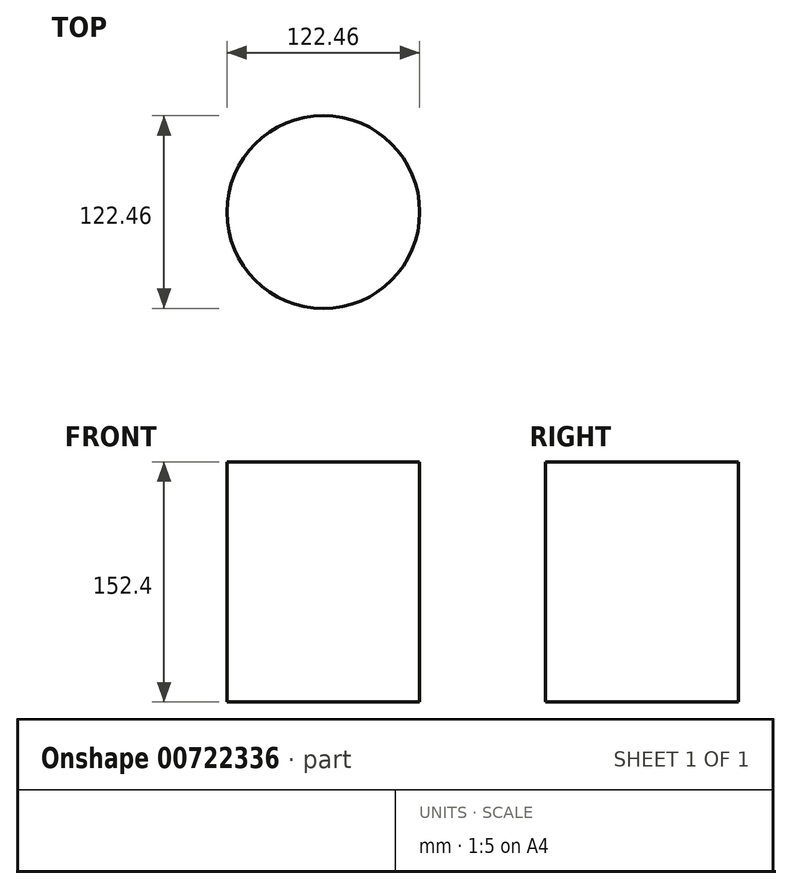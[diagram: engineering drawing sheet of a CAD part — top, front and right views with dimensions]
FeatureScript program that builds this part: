
annotation { "Feature Type Name" : "Feature", "Feature Type Description" : "" }
export const myFeature = defineFeature(function(context is Context, id is Id, definition is map)
    precondition{}
    {
        {
            var Q0;
            Q0=qCreatedBy(makeId("Top.planeOp"),FACE);
            var sketch = newSketch(context, id + "F0", { "sketchPlane" : qUnion([Q0])});
            skCircle(sketch, "E0", {"center": v(0, 0) * mm, "radius": 61.23 * mm});
            skSolve(sketch);
        }
        {
            var Q0;
            Q0=makeQuery(id+"F0.imprint","IMPRINT",FACE,{"disambiguationData":[TD([[makeQuery(id+"F0.imprint","IMPRINT",EDGE,{"derivedFrom":sQuery(id+"F0.wireOp",EDGE,"E0")}),1.0]])]});
            extrude(context, id + "F1", {"entities" : qUnion([Q0]), "depth" : 152.4 * mm, "offsetDistance" : 25.4 * mm});
        }
        {
            var Q0;
            Q0=qCreatedBy(makeId("Front.planeOp"),FACE);
            var sketch = newSketch(context, id + "F2", { "sketchPlane" : qUnion([Q0])});
            skLineSegment(sketch, "E1", {"start": v(-47.46, -54.9) * mm, "end": v(-17.83, -29.34) * mm});
            skLineSegment(sketch, "E2", {"start": v(-17.83, -29.34) * mm, "end": v(16.32, -24.4) * mm});
            skLineSegment(sketch, "E3", {"start": v(16.32, -24.4) * mm, "end": v(40.6, -36.21) * mm});
            skLineSegment(sketch, "E4", {"start": v(40.6, -36.21) * mm, "end": v(48.97, -60.05) * mm});
            skLineSegment(sketch, "E5", {"start": v(48.97, -60.05) * mm, "end": v(19.97, -67.35) * mm});
            skLineSegment(sketch, "E6", {"start": v(19.97, -67.35) * mm, "end": v(-21.9, -70.79) * mm});
            skLineSegment(sketch, "E7", {"start": v(-21.9, -70.79) * mm, "end": v(-48.75, -59.2) * mm});
            skLineSegment(sketch, "E8", {"start": v(-48.75, -59.2) * mm, "end": v(-63.14, -70.79) * mm});
            skLineSegment(sketch, "E9", {"start": v(-63.14, -70.79) * mm, "end": v(-63.14, -34.92) * mm});
            skLineSegment(sketch, "E10", {"start": v(-63.14, -34.92) * mm, "end": v(-47.46, -54.9) * mm});
            skSolve(sketch);
        }
        {
            var Q0;
            Q0=sQuery(id+"F2.wireOp",EDGE,"E3");
            var Q1;
            Q1=sQuery(id+"F2.wireOp",EDGE,"E2");
            var Q2;
            Q2=sQuery(id+"F2.wireOp",EDGE,"E6");
            var Q3;
            Q3=sQuery(id+"F2.wireOp",EDGE,"E8");
            var Q4;
            Q4=sQuery(id+"F2.wireOp",EDGE,"E9");
            var Q5;
            Q5=sQuery(id+"F2.wireOp",EDGE,"E4");
            var Q6;
            Q6=sQuery(id+"F2.wireOp",EDGE,"E5");
            var Q7;
            Q7=sQuery(id+"F2.wireOp",EDGE,"E1");
            var Q8;
            Q8=sQuery(id+"F2.wireOp",EDGE,"E7");
            var Q9;
            Q9=sQuery(id+"F2.wireOp",EDGE,"E10");
            extrude(context, id + "F3", {"bodyType" : ToolBodyType.SURFACE, "surfaceEntities" : qUnion([Q0, Q1, Q2, Q3, Q4, Q5, Q6, Q7, Q8, Q9]), "oppositeDirection" : true, "depth" : 25.4 * mm, "offsetDistance" : 25.4 * mm});
        }
    });
